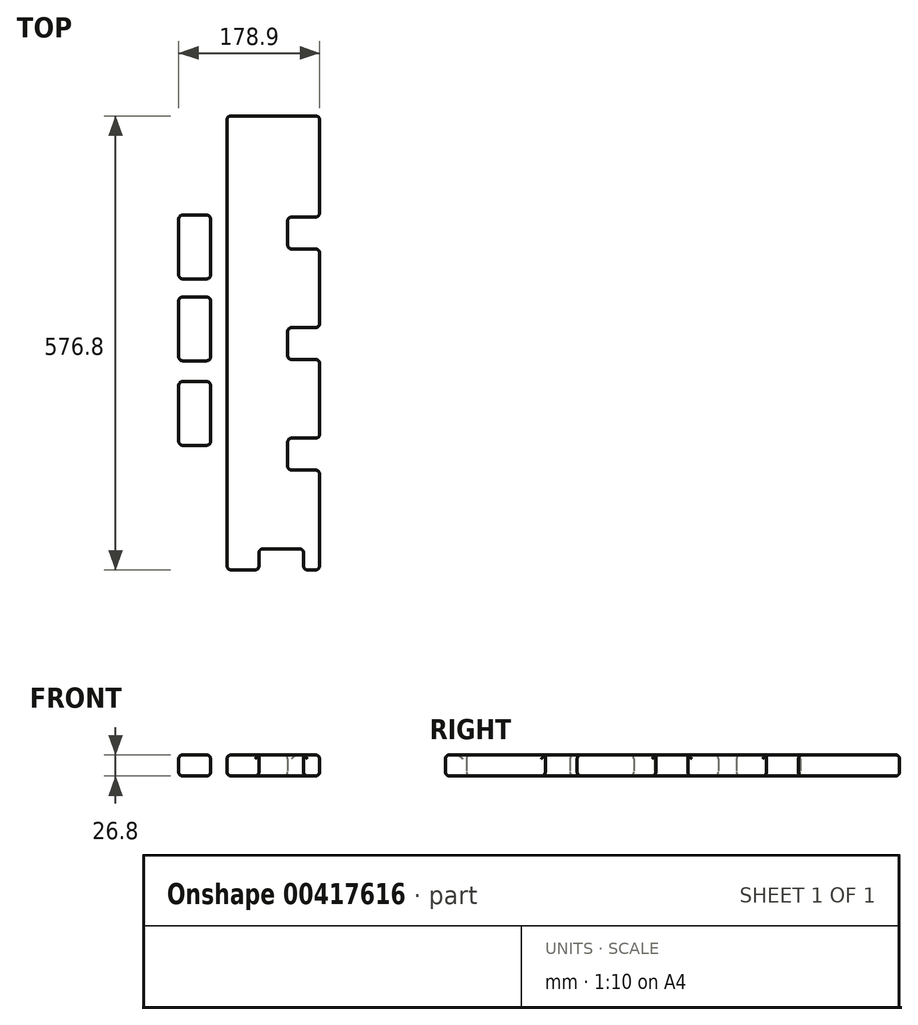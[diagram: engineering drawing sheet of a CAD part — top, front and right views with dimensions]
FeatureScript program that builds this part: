
annotation { "Feature Type Name" : "Feature", "Feature Type Description" : "" }
export const myFeature = defineFeature(function(context is Context, id is Id, definition is map)
    precondition{}
    {
        {
            var Q0;
            Q0=qCreatedBy(makeId("Top.planeOp"),FACE);
            var sketch = newSketch(context, id + "F0", { "sketchPlane" : qUnion([Q0])});
            skLineSegment(sketch, "E0.bottom", {"start": v(-94.48, 483.58) * mm, "end": v(-13.48, 483.58) * mm});
            skLineSegment(sketch, "E0.top", {"start": v(-53.98, -66.42) * mm, "end": v(2.72, -66.42) * mm});
            skLineSegment(sketch, "E0.left", {"start": v(-94.48, 483.58) * mm, "end": v(-94.48, -66.42) * mm});
            skLineSegment(sketch, "E1.top", {"start": v(-94.48, -93.22) * mm, "end": v(-53.98, -93.22) * mm});
            skLineSegment(sketch, "E1.left", {"start": v(-94.48, -66.42) * mm, "end": v(-94.48, -93.22) * mm});
            skLineSegment(sketch, "E1.right", {"start": v(-53.98, -66.42) * mm, "end": v(-53.98, -93.22) * mm});
            skPoint(sketch, "E2.firstSnap0", {"position": v(37.78, 349.1) * mm});
            skPoint(sketch, "E3.top.end.orphan", {"position": v(52.64, 99.1) * mm});
            skLineSegment(sketch, "E4.top", {"start": v(22.92, -93.22) * mm, "end": v(2.72, -93.22) * mm});
            skLineSegment(sketch, "E4.left", {"start": v(22.92, -66.42) * mm, "end": v(22.92, -93.22) * mm});
            skLineSegment(sketch, "E4.right", {"start": v(2.72, -66.42) * mm, "end": v(2.72, -93.22) * mm});
            skLineSegment(sketch, "E5.top", {"start": v(-13.48, 483.58) * mm, "end": v(22.92, 483.58) * mm});
            skPoint(sketch, "E6.orphan", {"position": v(52.64, 349.1) * mm});
            skPoint(sketch, "E7.top.start.orphan", {"position": v(22.92, 349.1) * mm});
            skPoint(sketch, "E8.right.start.orphan", {"position": v(-17.58, 349.1) * mm});
            skLineSegment(sketch, "E9.bottom", {"start": v(22.92, 33.58) * mm, "end": v(-17.58, 33.58) * mm});
            skLineSegment(sketch, "E9.top", {"start": v(22.92, 74.08) * mm, "end": v(-17.58, 74.08) * mm});
            skLineSegment(sketch, "E9.right", {"start": v(-17.58, 33.58) * mm, "end": v(-17.58, 74.08) * mm});
            skLineSegment(sketch, "E10.bottom", {"start": v(22.92, 174.08) * mm, "end": v(-17.58, 174.08) * mm});
            skLineSegment(sketch, "E10.top", {"start": v(22.92, 214.58) * mm, "end": v(-17.58, 214.58) * mm});
            skLineSegment(sketch, "E10.right", {"start": v(-17.58, 174.08) * mm, "end": v(-17.58, 214.58) * mm});
            skLineSegment(sketch, "E11.bottom", {"start": v(22.92, 314.58) * mm, "end": v(-17.58, 314.58) * mm});
            skLineSegment(sketch, "E11.top", {"start": v(22.92, 355.08) * mm, "end": v(-17.58, 355.08) * mm});
            skPoint(sketch, "E12.top.end.orphan", {"position": v(52.64, 383.58) * mm});
            skPoint(sketch, "E13.top.end.orphan", {"position": v(55.54, 174.08) * mm});
            skPoint(sketch, "E14.right.end.orphan", {"position": v(55.54, 33.58) * mm});
            skLineSegment(sketch, "E15", {"start": v(-17.58, 355.08) * mm, "end": v(-17.58, 314.58) * mm});
            skLineSegment(sketch, "E16", {"start": v(22.92, -66.42) * mm, "end": v(22.92, 33.58) * mm});
            skLineSegment(sketch, "E17.trimOffspring", {"start": v(22.92, 349.1) * mm, "end": v(22.92, 483.58) * mm});
            skLineSegment(sketch, "E18.trimOffspring", {"start": v(22.92, 214.58) * mm, "end": v(22.92, 314.58) * mm});
            skLineSegment(sketch, "E19.trimOffspring", {"start": v(22.92, 74.08) * mm, "end": v(22.92, 174.08) * mm});
            skLineSegment(sketch, "E20.bottom", {"start": v(-155.98, 357.56) * mm, "end": v(-115.48, 357.56) * mm});
            skLineSegment(sketch, "E20.top", {"start": v(-155.98, 276.56) * mm, "end": v(-115.48, 276.56) * mm});
            skLineSegment(sketch, "E20.left", {"start": v(-155.98, 357.56) * mm, "end": v(-155.98, 276.56) * mm});
            skLineSegment(sketch, "E20.right", {"start": v(-115.48, 357.56) * mm, "end": v(-115.48, 276.56) * mm});
            skLineSegment(sketch, "E21.bottom", {"start": v(-155.98, 253.48) * mm, "end": v(-115.48, 253.48) * mm});
            skLineSegment(sketch, "E21.top", {"start": v(-155.98, 172.48) * mm, "end": v(-115.48, 172.48) * mm});
            skLineSegment(sketch, "E21.left", {"start": v(-155.98, 253.48) * mm, "end": v(-155.98, 172.48) * mm});
            skLineSegment(sketch, "E21.right", {"start": v(-115.48, 253.48) * mm, "end": v(-115.48, 172.48) * mm});
            skLineSegment(sketch, "E22.bottom", {"start": v(-155.98, 146.08) * mm, "end": v(-115.48, 146.08) * mm});
            skLineSegment(sketch, "E22.top", {"start": v(-155.98, 65.08) * mm, "end": v(-115.48, 65.08) * mm});
            skLineSegment(sketch, "E22.left", {"start": v(-155.98, 146.08) * mm, "end": v(-155.98, 65.08) * mm});
            skLineSegment(sketch, "E22.right", {"start": v(-115.48, 146.08) * mm, "end": v(-115.48, 65.08) * mm});
            skSolve(sketch);
        }
        {
            var Q0;
            Q0 = qSketchRegion(id + "F0", true);
            extrude(context, id + "F1", {"entities" : qUnion([Q0]), "depth" : 26.8 * mm});
        }
        {
            var Q0;
            Q0=makeQuery(id+"F1.opExtrude","SWEPT_FACE",FACE,{"disambiguationData":[OSD([sQuery(id+"F0.wireOp",EDGE,"E18.trimOffspring")])]});
            var Q1;
            Q1=makeQuery(id+"F1.opExtrude","SWEPT_FACE",FACE,{"disambiguationData":[OSD([sQuery(id+"F0.wireOp",EDGE,"E17.trimOffspring")])]});
            var Q2;
            Q2=makeQuery(id+"F1.opExtrude","SWEPT_FACE",FACE,{"disambiguationData":[OSD([sQuery(id+"F0.wireOp",EDGE,"E15")])]});
            var Q3;
            Q3=makeQuery(id+"F1.opExtrude","SWEPT_FACE",FACE,{"disambiguationData":[OSD([sQuery(id+"F0.wireOp",EDGE,"E10.right")])]});
            var Q4;
            Q4=makeQuery(id+"F1.opExtrude","SWEPT_FACE",FACE,{"disambiguationData":[OSD([sQuery(id+"F0.wireOp",EDGE,"E19.trimOffspring")])]});
            var Q5;
            Q5=makeQuery(id+"F1.opExtrude","SWEPT_FACE",FACE,{"disambiguationData":[OSD([sQuery(id+"F0.wireOp",EDGE,"E9.right")])]});
            var Q6;
            Q6=makeQuery(id+"F1.opExtrude","SWEPT_FACE",FACE,{"disambiguationData":[OSD([sQuery(id+"F0.wireOp",EDGE,"E4.left"),sQuery(id+"F0.wireOp",EDGE,"E16")])]});
            var Q7;
            Q7=makeQuery(id+"F1.opExtrude","SWEPT_FACE",FACE,{"disambiguationData":[OSD([sQuery(id+"F0.wireOp",EDGE,"E0.top")])]});
            var Q8;
            Q8=makeQuery(id+"F1.opExtrude","SWEPT_FACE",FACE,{"disambiguationData":[OSD([sQuery(id+"F0.wireOp",EDGE,"E4.top")])]});
            var Q9;
            Q9=makeQuery(id+"F1.opExtrude","SWEPT_FACE",FACE,{"disambiguationData":[OSD([sQuery(id+"F0.wireOp",EDGE,"E1.top")])]});
            var Q10;
            Q10=makeQuery(id+"F1.opExtrude","SWEPT_FACE",FACE,{"disambiguationData":[OSD([sQuery(id+"F0.wireOp",EDGE,"E22.top")])]});
            var Q11;
            Q11=makeQuery(id+"F1.opExtrude","SWEPT_FACE",FACE,{"disambiguationData":[OSD([sQuery(id+"F0.wireOp",EDGE,"E22.left")])]});
            var Q12;
            Q12=makeQuery(id+"F1.opExtrude","SWEPT_FACE",FACE,{"disambiguationData":[OSD([sQuery(id+"F0.wireOp",EDGE,"E21.left")])]});
            var Q13;
            Q13=makeQuery(id+"F1.opExtrude","SWEPT_FACE",FACE,{"disambiguationData":[OSD([sQuery(id+"F0.wireOp",EDGE,"E20.left")])]});
            var Q14;
            Q14=makeQuery(id+"F1.opExtrude","SWEPT_FACE",FACE,{"disambiguationData":[OSD([sQuery(id+"F0.wireOp",EDGE,"E0.bottom"),sQuery(id+"F0.wireOp",EDGE,"E5.top")])]});
            var Q15;
            Q15=makeQuery(id+"F1.opExtrude","SWEPT_FACE",FACE,{"disambiguationData":[OSD([sQuery(id+"F0.wireOp",EDGE,"E20.bottom")])]});
            var Q16;
            Q16=makeQuery(id+"F1.opExtrude","SWEPT_EDGE",EDGE,{"disambiguationData":[OSD([sQuery(id+"F0.wireOp",EDGE,"E22.bottom"),sQuery(id+"F0.wireOp",EDGE,"E22.right")])]});
            var Q17;
            Q17=makeQuery(id+"F1.opExtrude","CAP_EDGE",EDGE,{"disambiguationData":[OSD([sQuery(id+"F0.wireOp",EDGE,"E22.right")])],"isStart":false});
            var Q18;
            Q18=makeQuery(id+"F1.opExtrude","CAP_EDGE",EDGE,{"disambiguationData":[OSD([sQuery(id+"F0.wireOp",EDGE,"E21.right")])],"isStart":false});
            var Q19;
            Q19=makeQuery(id+"F1.opExtrude","CAP_EDGE",EDGE,{"disambiguationData":[OSD([sQuery(id+"F0.wireOp",EDGE,"E20.right")])],"isStart":false});
            var Q20;
            Q20=makeQuery(id+"F1.opExtrude","CAP_EDGE",EDGE,{"disambiguationData":[OSD([sQuery(id+"F0.wireOp",EDGE,"E21.top")])],"isStart":false});
            var Q21;
            Q21=makeQuery(id+"F1.opExtrude","CAP_EDGE",EDGE,{"disambiguationData":[OSD([sQuery(id+"F0.wireOp",EDGE,"E22.bottom")])],"isStart":false});
            var Q22;
            Q22=makeQuery(id+"F1.opExtrude","CAP_EDGE",EDGE,{"disambiguationData":[OSD([sQuery(id+"F0.wireOp",EDGE,"E21.bottom")])],"isStart":false});
            var Q23;
            Q23=makeQuery(id+"F1.opExtrude","SWEPT_EDGE",EDGE,{"disambiguationData":[OSD([sQuery(id+"F0.wireOp",EDGE,"E21.bottom"),sQuery(id+"F0.wireOp",EDGE,"E21.right")])]});
            var Q24;
            Q24=makeQuery(id+"F1.opExtrude","CAP_EDGE",EDGE,{"disambiguationData":[OSD([sQuery(id+"F0.wireOp",EDGE,"E0.left"),sQuery(id+"F0.wireOp",EDGE,"E1.left")])],"isStart":false});
            var Q25;
            Q25=makeQuery(id+"F1.opExtrude","CAP_EDGE",EDGE,{"disambiguationData":[OSD([sQuery(id+"F0.wireOp",EDGE,"E0.left"),sQuery(id+"F0.wireOp",EDGE,"E1.left")])],"isStart":true});
            var Q26;
            Q26=makeQuery(id+"F1.opExtrude","CAP_EDGE",EDGE,{"disambiguationData":[OSD([sQuery(id+"F0.wireOp",EDGE,"E20.left")])],"isStart":true});
            var Q27;
            Q27=makeQuery(id+"F1.opExtrude","CAP_EDGE",EDGE,{"disambiguationData":[OSD([sQuery(id+"F0.wireOp",EDGE,"E21.left")])],"isStart":true});
            var Q28;
            Q28=makeQuery(id+"F1.opExtrude","CAP_EDGE",EDGE,{"disambiguationData":[OSD([sQuery(id+"F0.wireOp",EDGE,"E21.bottom")])],"isStart":true});
            var Q29;
            Q29=makeQuery(id+"F1.opExtrude","CAP_EDGE",EDGE,{"disambiguationData":[OSD([sQuery(id+"F0.wireOp",EDGE,"E20.bottom")])],"isStart":true});
            var Q30;
            Q30=makeQuery(id+"F1.opExtrude","CAP_EDGE",EDGE,{"disambiguationData":[OSD([sQuery(id+"F0.wireOp",EDGE,"E0.bottom"),sQuery(id+"F0.wireOp",EDGE,"E5.top")])],"isStart":true});
            var Q31;
            Q31=makeQuery(id+"F1.opExtrude","SWEPT_EDGE",EDGE,{"disambiguationData":[OSD([sQuery(id+"F0.wireOp",EDGE,"E11.top"),sQuery(id+"F0.wireOp",EDGE,"E17.trimOffspring")])]});
            var Q32;
            Q32=makeQuery(id+"F1.opExtrude","CAP_EDGE",EDGE,{"disambiguationData":[OSD([sQuery(id+"F0.wireOp",EDGE,"E17.trimOffspring")])],"isStart":true});
            var Q33;
            Q33=makeQuery(id+"F1.opExtrude","CAP_EDGE",EDGE,{"disambiguationData":[OSD([sQuery(id+"F0.wireOp",EDGE,"E18.trimOffspring")])],"isStart":true});
            var Q34;
            Q34=makeQuery(id+"F1.opExtrude","SWEPT_EDGE",EDGE,{"disambiguationData":[OSD([sQuery(id+"F0.wireOp",EDGE,"E11.bottom"),sQuery(id+"F0.wireOp",EDGE,"E18.trimOffspring")])]});
            var Q35;
            Q35=makeQuery(id+"F1.opExtrude","CAP_EDGE",EDGE,{"disambiguationData":[OSD([sQuery(id+"F0.wireOp",EDGE,"E19.trimOffspring")])],"isStart":true});
            var Q36;
            Q36=makeQuery(id+"F1.opExtrude","SWEPT_EDGE",EDGE,{"disambiguationData":[OSD([sQuery(id+"F0.wireOp",EDGE,"E10.bottom"),sQuery(id+"F0.wireOp",EDGE,"E19.trimOffspring")])]});
            var Q37;
            Q37=makeQuery(id+"F1.opExtrude","CAP_EDGE",EDGE,{"disambiguationData":[OSD([sQuery(id+"F0.wireOp",EDGE,"E10.bottom")])],"isStart":true});
            var Q38;
            Q38=makeQuery(id+"F1.opExtrude","CAP_EDGE",EDGE,{"disambiguationData":[OSD([sQuery(id+"F0.wireOp",EDGE,"E9.top")])],"isStart":false});
            var Q39;
            Q39=makeQuery(id+"F1.opExtrude","CAP_EDGE",EDGE,{"disambiguationData":[OSD([sQuery(id+"F0.wireOp",EDGE,"E9.right")])],"isStart":true});
            var Q40;
            Q40=makeQuery(id+"F1.opExtrude","CAP_EDGE",EDGE,{"disambiguationData":[OSD([sQuery(id+"F0.wireOp",EDGE,"E9.bottom")])],"isStart":true});
            var Q41;
            Q41=makeQuery(id+"F1.opExtrude","CAP_EDGE",EDGE,{"disambiguationData":[OSD([sQuery(id+"F0.wireOp",EDGE,"E4.left"),sQuery(id+"F0.wireOp",EDGE,"E16")])],"isStart":true});
            var Q42;
            Q42=makeQuery(id+"F1.opExtrude","CAP_EDGE",EDGE,{"disambiguationData":[OSD([sQuery(id+"F0.wireOp",EDGE,"E11.top")])],"isStart":false});
            var Q43;
            Q43=makeQuery(id+"F1.opExtrude","CAP_EDGE",EDGE,{"disambiguationData":[OSD([sQuery(id+"F0.wireOp",EDGE,"E11.bottom")])],"isStart":true});
            var Q44;
            Q44=makeQuery(id+"F1.opExtrude","CAP_EDGE",EDGE,{"disambiguationData":[OSD([sQuery(id+"F0.wireOp",EDGE,"E20.right")])],"isStart":true});
            var Q45;
            Q45=makeQuery(id+"F1.opExtrude","CAP_EDGE",EDGE,{"disambiguationData":[OSD([sQuery(id+"F0.wireOp",EDGE,"E21.right")])],"isStart":true});
            var Q46;
            Q46=makeQuery(id+"F1.opExtrude","CAP_FACE",FACE,{"disambiguationData":[OSD([sQuery(id+"F0.wireOp",EDGE,"E22.bottom"),sQuery(id+"F0.wireOp",EDGE,"E22.top"),sQuery(id+"F0.wireOp",EDGE,"E22.left"),sQuery(id+"F0.wireOp",EDGE,"E22.right")])],"isStart":true});
            var Q47;
            Q47=makeQuery(id+"F1.opExtrude","SWEPT_EDGE",EDGE,{"disambiguationData":[OSD([sQuery(id+"F0.wireOp",EDGE,"E22.top"),sQuery(id+"F0.wireOp",EDGE,"E22.left")])]});
            var Q48;
            Q48=makeQuery(id+"F1.opExtrude","CAP_FACE",FACE,{"disambiguationData":[OSD([sQuery(id+"F0.wireOp",EDGE,"E21.bottom"),sQuery(id+"F0.wireOp",EDGE,"E21.top"),sQuery(id+"F0.wireOp",EDGE,"E21.left"),sQuery(id+"F0.wireOp",EDGE,"E21.right")])],"isStart":true});
            var Q49;
            Q49=makeQuery(id+"F1.opExtrude","SWEPT_FACE",FACE,{"disambiguationData":[OSD([sQuery(id+"F0.wireOp",EDGE,"E20.top")])]});
            var Q50;
            Q50=makeQuery(id+"F1.opExtrude","SWEPT_EDGE",EDGE,{"disambiguationData":[OSD([sQuery(id+"F0.wireOp",EDGE,"E21.top"),sQuery(id+"F0.wireOp",EDGE,"E21.right")])]});
            var Q51;
            Q51=makeQuery(id+"F1.opExtrude","SWEPT_EDGE",EDGE,{"disambiguationData":[OSD([sQuery(id+"F0.wireOp",EDGE,"E22.top"),sQuery(id+"F0.wireOp",EDGE,"E22.right")])]});
            var Q52;
            Q52=makeQuery(id+"F1.opExtrude","CAP_EDGE",EDGE,{"disambiguationData":[OSD([sQuery(id+"F0.wireOp",EDGE,"E22.top")])],"isStart":true});
            var Q53;
            Q53=makeQuery(id+"F1.opExtrude","SWEPT_EDGE",EDGE,{"disambiguationData":[OSD([sQuery(id+"F0.wireOp",EDGE,"E20.top"),sQuery(id+"F0.wireOp",EDGE,"E20.right")])]});
            var Q54;
            Q54=makeQuery(id+"F1.opExtrude","SWEPT_EDGE",EDGE,{"disambiguationData":[OSD([sQuery(id+"F0.wireOp",EDGE,"E20.top"),sQuery(id+"F0.wireOp",EDGE,"E20.left")])]});
            var Q55;
            Q55=makeQuery(id+"F1.opExtrude","SWEPT_FACE",FACE,{"disambiguationData":[OSD([sQuery(id+"F0.wireOp",EDGE,"E20.right")])]});
            var Q56;
            Q56=makeQuery(id+"F1.opExtrude","CAP_EDGE",EDGE,{"disambiguationData":[OSD([sQuery(id+"F0.wireOp",EDGE,"E21.top")])],"isStart":true});
            var Q57;
            Q57=makeQuery(id+"F1.opExtrude","CAP_EDGE",EDGE,{"disambiguationData":[OSD([sQuery(id+"F0.wireOp",EDGE,"E20.top")])],"isStart":true});
            var Q58;
            Q58=makeQuery(id+"F1.opExtrude","CAP_FACE",FACE,{"disambiguationData":[OSD([sQuery(id+"F0.wireOp",EDGE,"E0.bottom"),sQuery(id+"F0.wireOp",EDGE,"E0.top"),sQuery(id+"F0.wireOp",EDGE,"E0.left"),sQuery(id+"F0.wireOp",EDGE,"E1.top"),sQuery(id+"F0.wireOp",EDGE,"E1.left"),sQuery(id+"F0.wireOp",EDGE,"E1.right"),sQuery(id+"F0.wireOp",EDGE,"E4.top"),sQuery(id+"F0.wireOp",EDGE,"E4.left"),sQuery(id+"F0.wireOp",EDGE,"E4.right"),sQuery(id+"F0.wireOp",EDGE,"E5.top"),sQuery(id+"F0.wireOp",EDGE,"E9.bottom"),sQuery(id+"F0.wireOp",EDGE,"E9.top"),sQuery(id+"F0.wireOp",EDGE,"E9.right"),sQuery(id+"F0.wireOp",EDGE,"E10.bottom"),sQuery(id+"F0.wireOp",EDGE,"E10.top"),sQuery(id+"F0.wireOp",EDGE,"E10.right"),sQuery(id+"F0.wireOp",EDGE,"E11.bottom"),sQuery(id+"F0.wireOp",EDGE,"E11.top"),sQuery(id+"F0.wireOp",EDGE,"E15"),sQuery(id+"F0.wireOp",EDGE,"E16"),sQuery(id+"F0.wireOp",EDGE,"E17.trimOffspring"),sQuery(id+"F0.wireOp",EDGE,"E18.trimOffspring"),sQuery(id+"F0.wireOp",EDGE,"E19.trimOffspring")])],"isStart":true});
            fillet(context, id + "F2", {"entities" : qUnion([Q0, Q1, Q2, Q3, Q4, Q5, Q6, Q7, Q8, Q9, Q10, Q11, Q12, Q13, Q14, Q15, Q16, Q17, Q18, Q19, Q20, Q21, Q22, Q23, Q24, Q25, Q26, Q27, Q28, Q29, Q30, Q31, Q32, Q33, Q34, Q35, Q36, Q37, Q38, Q39, Q40, Q41, Q42, Q43, Q44, Q45, Q46, Q47, Q48, Q49, Q50, Q51, Q52, Q53, Q54, Q55, Q56, Q57, Q58]), "radius" : 5 * mm, "tangentPropagation" : true, "allowEdgeOverflow" : false});
        }
    });
